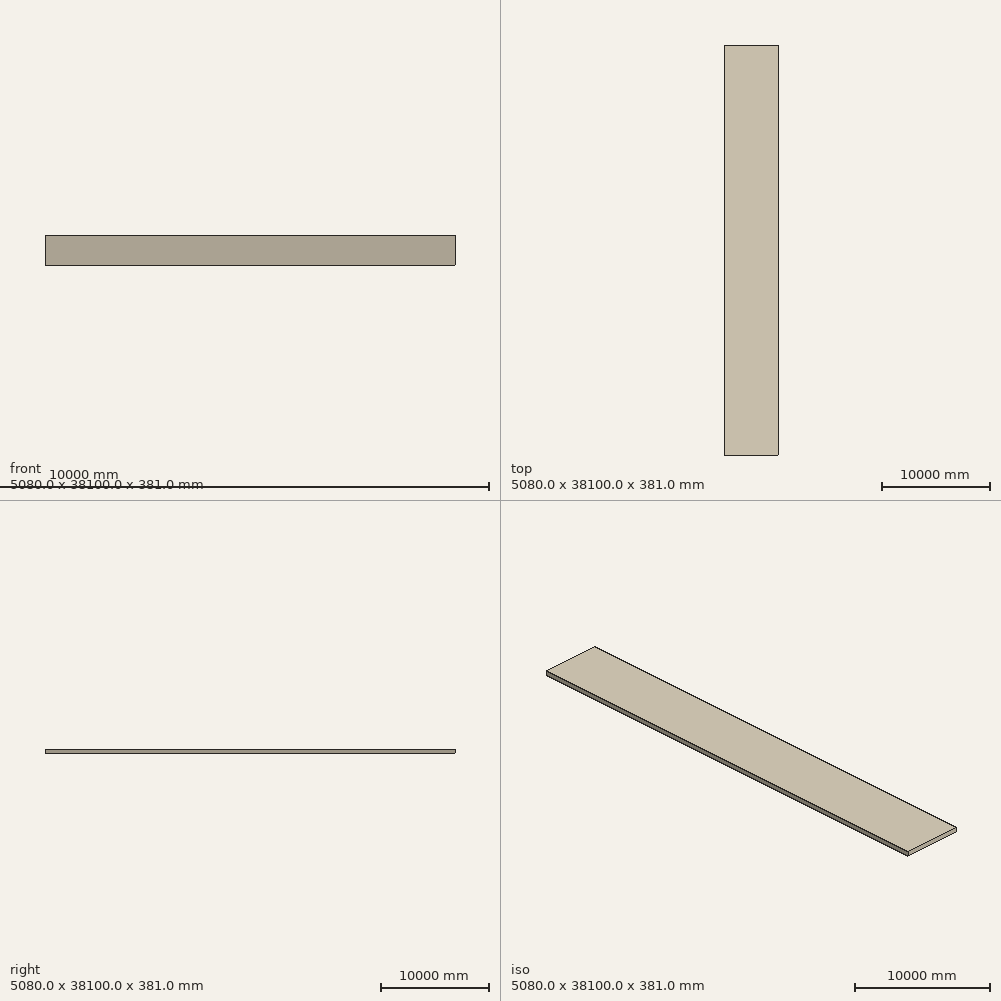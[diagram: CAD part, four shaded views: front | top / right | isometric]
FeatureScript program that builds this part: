
annotation { "Feature Type Name" : "Feature", "Feature Type Description" : "" }
export const myFeature = defineFeature(function(context is Context, id is Id, definition is map)
    precondition{}
    {
        {
            var Q0;
            Q0=qCreatedBy(makeId("Top.planeOp"),FACE);
            var sketch = newSketch(context, id + "F0", { "sketchPlane" : qUnion([Q0])});
            skLineSegment(sketch, "E0.bottom", {"start": v(-35.9, 38001.64) * mm, "end": v(5044.1, 38001.64) * mm});
            skLineSegment(sketch, "E0.top", {"start": v(-35.9, -98.36) * mm, "end": v(5044.1, -98.36) * mm});
            skLineSegment(sketch, "E0.left", {"start": v(-35.9, 38001.64) * mm, "end": v(-35.9, -98.36) * mm});
            skLineSegment(sketch, "E0.right", {"start": v(5044.1, 38001.64) * mm, "end": v(5044.1, -98.36) * mm});
            skSolve(sketch);
        }
        {
            var Q0;
            Q0 = qSketchRegion(id + "F0", true);
            extrude(context, id + "F1", {"entities" : qUnion([Q0]), "depth" : 381 * mm, "offsetDistance" : 25.4 * mm});
        }
    });
